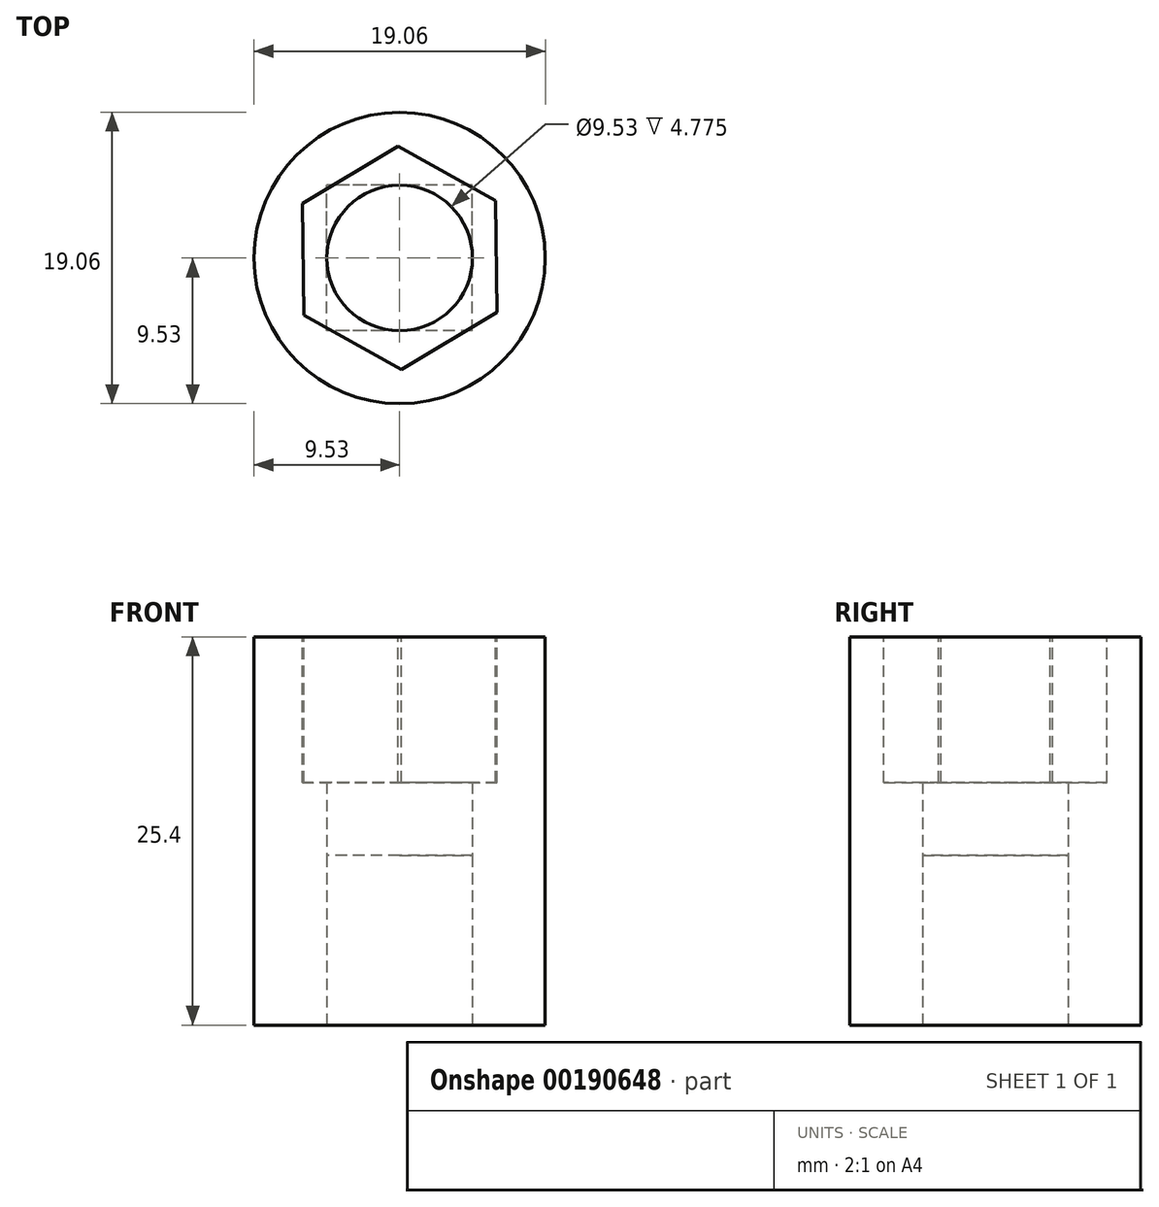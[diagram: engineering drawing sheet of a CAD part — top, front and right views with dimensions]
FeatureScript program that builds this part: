
annotation { "Feature Type Name" : "Feature", "Feature Type Description" : "" }
export const myFeature = defineFeature(function(context is Context, id is Id, definition is map)
    precondition{}
    {
        {
            var Q0;
            Q0=qCreatedBy(makeId("Top.planeOp"),FACE);
            var sketch = newSketch(context, id + "F0", { "sketchPlane" : qUnion([Q0])});
            skCircle(sketch, "E0", {"center": v(0, 0) * mm, "radius": 9.53 * mm});
            skSolve(sketch);
        }
        {
            var Q0;
            Q0 = qSketchRegion(id + "F0", true);
            extrude(context, id + "F1", {"entities" : qUnion([Q0]), "depth" : 25.4 * mm});
        }
        {
            var Q0;
            Q0=qCreatedBy(makeId("Top.planeOp"),FACE);
            var sketch = newSketch(context, id + "F2", { "sketchPlane" : qUnion([Q0])});
            skLineSegment(sketch, "E1.bottom", {"start": v(4.76, -4.76) * mm, "end": v(-4.76, -4.76) * mm});
            skLineSegment(sketch, "E1.top", {"start": v(4.76, 4.76) * mm, "end": v(-4.76, 4.76) * mm});
            skLineSegment(sketch, "E1.left", {"start": v(4.76, -4.76) * mm, "end": v(4.76, 4.76) * mm});
            skLineSegment(sketch, "E1.right", {"start": v(-4.76, -4.76) * mm, "end": v(-4.76, 4.76) * mm});
            skPoint(sketch, "E1.middle", {"position": v(0, 0) * mm});
            skCircle(sketch, "E2", {"center": v(0, 0) * mm, "radius": 4.76 * mm});
            skSolve(sketch);
        }
        {
            var Q0;
            {var subQ0=sQuery(id+"F2.wireOp",EDGE,"E2");var subQ1=makeQuery(id+"F2.imprint","INTERSECT",VERTEX,{"derivedFrom":[sQuery(id+"F2.wireOp",EDGE,"E1.top"),subQ0]});Q0=makeQuery(id+"F2.imprint","IMPRINT",FACE,{"disambiguationData":[TD([[makeQuery(id+"F2.imprint","IMPRINT",EDGE,{"disambiguationData":[TD([[subQ1,1.0]])],"derivedFrom":subQ0}),1.0]])]});}
            extrude(context, id + "F3", {"entities" : qUnion([Q0]), "operationType" : NewBodyOperationType.REMOVE, "endBound" : BoundingType.THROUGH_ALL, "depth" : 25.4 * mm});
        }
        {
            var Q0;
            Q0 = qSketchRegion(id + "F2", true);
            extrude(context, id + "F4", {"entities" : qUnion([Q0]), "operationType" : NewBodyOperationType.REMOVE, "depth" : 11.1 * mm});
        }
        {
            var Q0;
            Q0=makeQuery(id+"F1.opExtrude","CAP_FACE",FACE,{"disambiguationData":[OSD([sQuery(id+"F0.wireOp",EDGE,"E0")])],"isStart":false});
            var sketch = newSketch(context, id + "F5", { "sketchPlane" : qUnion([Q0])});
            skCircle(sketch, "E3.cCircle", {"center": v(0, 0) * mm, "radius": 6.32 * mm, "construction": true});
            skLineSegment(sketch, "E3.0", {"start": v(6.38, -3.56) * mm, "end": v(0.1, -7.3) * mm});
            skLineSegment(sketch, "E3.1", {"start": v(0.1, -7.3) * mm, "end": v(-6.27, -3.74) * mm});
            skLineSegment(sketch, "E3.2", {"start": v(-6.27, -3.74) * mm, "end": v(-6.38, 3.56) * mm});
            skLineSegment(sketch, "E3.3", {"start": v(-6.38, 3.56) * mm, "end": v(-0.1, 7.3) * mm});
            skLineSegment(sketch, "E3.4", {"start": v(-0.1, 7.3) * mm, "end": v(6.27, 3.74) * mm});
            skLineSegment(sketch, "E3.5", {"start": v(6.27, 3.74) * mm, "end": v(6.38, -3.56) * mm});
            skPoint(sketch, "E3.0.midPoint", {"position": v(3.24, -5.43) * mm});
            skSolve(sketch);
        }
        {
            var Q0;
            Q0 = qSketchRegion(id + "F5", true);
            extrude(context, id + "F6", {"entities" : qUnion([Q0]), "operationType" : NewBodyOperationType.REMOVE, "oppositeDirection" : true, "depth" : 9.52 * mm});
        }
    });
